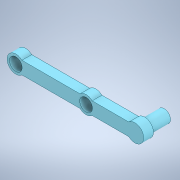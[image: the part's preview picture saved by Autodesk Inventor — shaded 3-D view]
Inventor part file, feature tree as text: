
AUTODESK INVENTOR PART (.ipt)
format: ipt  version: 2022 (Build 260153000, 153)  size: 139,776 bytes
history: native  units: in
note: dims shown in document units (in); Inventor stores cm internally (conversion verified against a paired STEP export)
features: extrude x2, sketch x1
ambient origin geometry x8: Origin, YZ Plane, XZ Plane, XY Plane, X Axis, Y Axis, Z Axis, Center Point
bodies: Solid1 (feature_tree)
feature tree (3):
  sketch  "Sketch2"  dims[d0=0.1969in d1=0.0in d2=0.3937in d3=0.0in d4=0.9843in d5=1.4173in d6=0.2559in d7=0.3543in d8=0.2559in]
  extrude  "Extrusion1"  Depth=0.3937in TaperAngle=0.0deg
  extrude  "Extrusion2"  Depth=0.2559in
